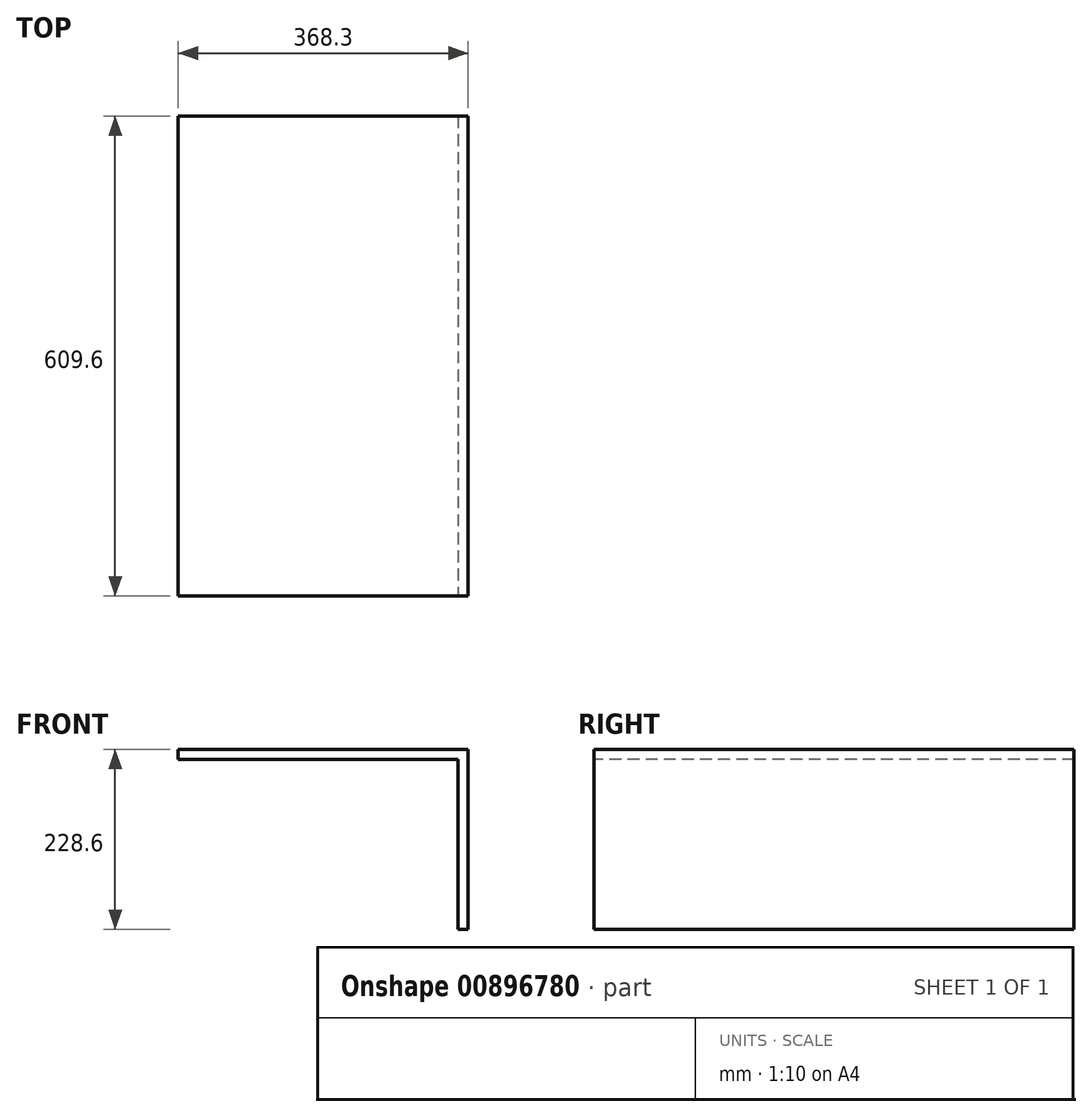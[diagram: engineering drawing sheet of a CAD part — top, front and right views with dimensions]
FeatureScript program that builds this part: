
annotation { "Feature Type Name" : "Feature", "Feature Type Description" : "" }
export const myFeature = defineFeature(function(context is Context, id is Id, definition is map)
    precondition{}
    {
        {
            var Q0;
            Q0=qCreatedBy(makeId("Front.planeOp"),FACE);
            var sketch = newSketch(context, id + "F0", { "sketchPlane" : qUnion([Q0])});
            skLineSegment(sketch, "E0", {"start": v(0, 0) * mm, "end": v(0, 228.6) * mm});
            skLineSegment(sketch, "E1", {"start": v(0, 228.6) * mm, "end": v(-368.3, 228.6) * mm});
            skLineSegment(sketch, "E2", {"start": v(-368.3, 228.6) * mm, "end": v(-368.3, 215.9) * mm});
            skLineSegment(sketch, "E3", {"start": v(-368.3, 215.9) * mm, "end": v(-12.7, 215.9) * mm});
            skLineSegment(sketch, "E4", {"start": v(-12.7, 215.9) * mm, "end": v(-12.7, 0) * mm});
            skLineSegment(sketch, "E5", {"start": v(-12.7, 0) * mm, "end": v(0, 0) * mm});
            skSolve(sketch);
        }
        {
            var Q0;
            Q0=makeQuery(id+"F0.imprint","IMPRINT",FACE,{"disambiguationData":[TD([[makeQuery(id+"F0.imprint","IMPRINT",EDGE,{"derivedFrom":sQuery(id+"F0.wireOp",EDGE,"E0")}),1.0]])]});
            extrude(context, id + "F1", {"entities" : qUnion([Q0]), "oppositeDirection" : true, "depth" : 609.6 * mm, "offsetDistance" : 25.4 * mm});
        }
    });
